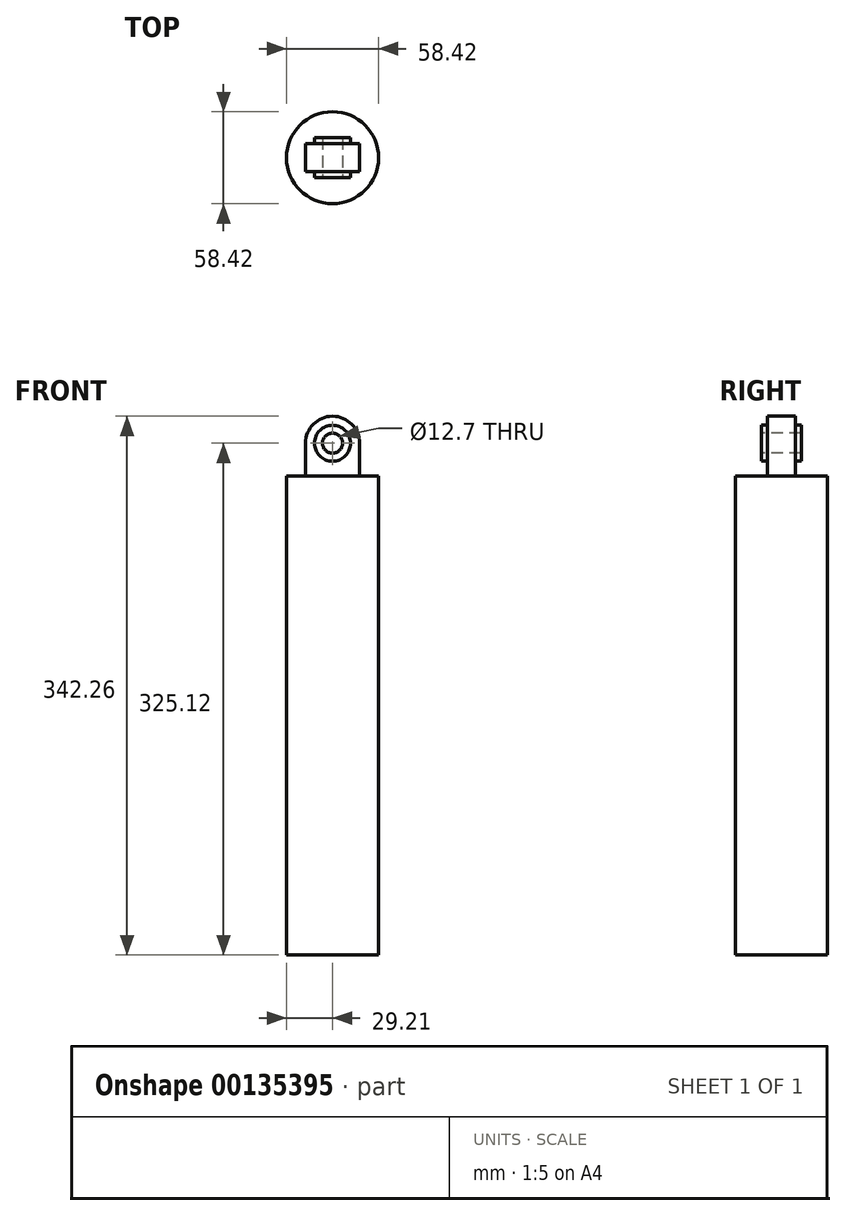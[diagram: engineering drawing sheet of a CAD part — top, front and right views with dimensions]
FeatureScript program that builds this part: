
annotation { "Feature Type Name" : "Feature", "Feature Type Description" : "" }
export const myFeature = defineFeature(function(context is Context, id is Id, definition is map)
    precondition{}
    {
        {
            var Q0;
            Q0=qCreatedBy(makeId("Top.planeOp"),FACE);
            var sketch = newSketch(context, id + "F0", { "sketchPlane" : qUnion([Q0])});
            skCircle(sketch, "E0", {"center": v(0, 0) * mm, "radius": 29.2 * mm});
            skSolve(sketch);
        }
        {
            var Q0;
            Q0=makeQuery(id+"F0.imprint","IMPRINT",FACE,{"disambiguationData":[TD([[makeQuery(id+"F0.imprint","IMPRINT",EDGE,{"derivedFrom":sQuery(id+"F0.wireOp",EDGE,"E0")}),1.0]])]});
            extrude(context, id + "F1", {"entities" : qUnion([Q0]), "depth" : 304.16 * mm});
        }
        {
            var Q0;
            Q0=makeQuery(id+"F1.opExtrude","CAP_FACE",FACE,{"disambiguationData":[OSD([sQuery(id+"F0.wireOp",EDGE,"E0")])],"isStart":false});
            var sketch = newSketch(context, id + "F2", { "sketchPlane" : qUnion([Q0])});
            skLineSegment(sketch, "E1.bottom", {"start": v(-17.14, -8.9) * mm, "end": v(17.15, -8.9) * mm});
            skLineSegment(sketch, "E1.top", {"start": v(-17.15, 8.9) * mm, "end": v(17.14, 8.9) * mm});
            skLineSegment(sketch, "E1.left", {"start": v(-17.14, -8.9) * mm, "end": v(-17.15, 8.9) * mm});
            skLineSegment(sketch, "E1.right", {"start": v(17.15, -8.9) * mm, "end": v(17.14, 8.9) * mm});
            skPoint(sketch, "E1.middle", {"position": v(0, 0) * mm});
            skSolve(sketch);
        }
        {
            var Q0;
            Q0=makeQuery(id+"F2.imprint","IMPRINT",FACE,{"disambiguationData":[TD([[makeQuery(id+"F2.imprint","IMPRINT",EDGE,{"derivedFrom":sQuery(id+"F2.wireOp",EDGE,"E1.bottom")}),1.0]])]});
            extrude(context, id + "F3", {"entities" : qUnion([Q0]), "operationType" : NewBodyOperationType.ADD, "depth" : 38.1 * mm});
        }
        {
            var Q0;
            Q0=makeQuery(id+"F3.opExtrude","CAP_EDGE",EDGE,{"disambiguationData":[OSD([sQuery(id+"F2.wireOp",EDGE,"E1.right")])],"isStart":false});
            var Q1;
            Q1=makeQuery(id+"F3.opExtrude","CAP_EDGE",EDGE,{"disambiguationData":[OSD([sQuery(id+"F2.wireOp",EDGE,"E1.left")])],"isStart":false});
            fillet(context, id + "F4", {"entities" : qUnion([Q0, Q1]), "radius" : 17.14 * mm, "tangentPropagation" : true, "allowEdgeOverflow" : false});
        }
        {
            var Q0;
            Q0=makeQuery(id+"F3.opExtrude","SWEPT_FACE",FACE,{"disambiguationData":[OSD([sQuery(id+"F2.wireOp",EDGE,"E1.top")])]});
            var sketch = newSketch(context, id + "F5", { "sketchPlane" : qUnion([Q0])});
            skCircle(sketch, "E2", {"center": v(0, 325.12) * mm, "radius": 11.43 * mm});
            skSolve(sketch);
        }
        {
            var Q0;
            Q0=qSketchRegion(id+"F5",true);
            extrude(context, id + "F6", {"entities" : qUnion([Q0]), "operationType" : NewBodyOperationType.ADD, "depth" : 3.8 * mm});
        }
        {
            var Q0;
            Q0=makeQuery(id+"F3.opExtrude","SWEPT_FACE",FACE,{"disambiguationData":[OSD([sQuery(id+"F2.wireOp",EDGE,"E1.bottom")])]});
            var sketch = newSketch(context, id + "F7", { "sketchPlane" : qUnion([Q0])});
            skCircle(sketch, "E3", {"center": v(0, 325.12) * mm, "radius": 11.43 * mm});
            skSolve(sketch);
        }
        {
            var Q0;
            Q0=makeQuery(id+"F7.imprint","IMPRINT",FACE,{"disambiguationData":[TD([[makeQuery(id+"F7.imprint","IMPRINT",EDGE,{"derivedFrom":sQuery(id+"F7.wireOp",EDGE,"E3")}),1.0]])]});
            extrude(context, id + "F8", {"entities" : qUnion([Q0]), "operationType" : NewBodyOperationType.ADD, "depth" : 3.8 * mm});
        }
        {
            var Q0;
            Q0=makeQuery(id+"F8.opExtrude","CAP_FACE",FACE,{"disambiguationData":[OSD([sQuery(id+"F7.wireOp",EDGE,"E3")])],"isStart":false});
            var sketch = newSketch(context, id + "F9", { "sketchPlane" : qUnion([Q0])});
            skCircle(sketch, "E4", {"center": v(0, 325.12) * mm, "radius": 6.35 * mm});
            skSolve(sketch);
        }
        {
            var Q0;
            Q0=qSketchRegion(id+"F9",true);
            extrude(context, id + "F10", {"entities" : qUnion([Q0]), "operationType" : NewBodyOperationType.REMOVE, "oppositeDirection" : true, "depth" : 38.1 * mm});
        }
    });
